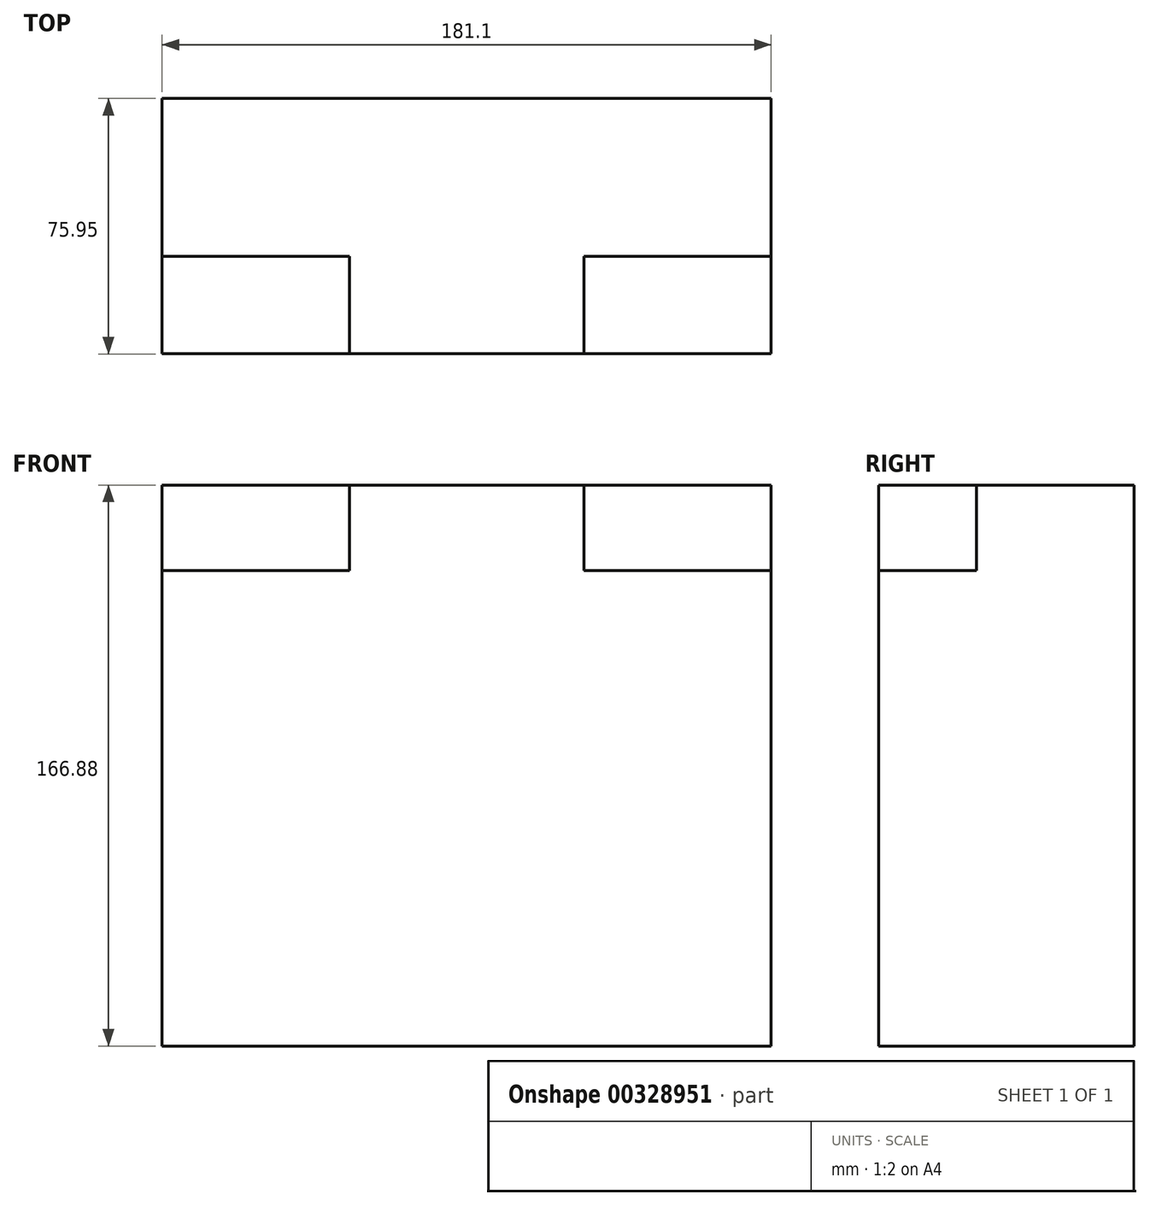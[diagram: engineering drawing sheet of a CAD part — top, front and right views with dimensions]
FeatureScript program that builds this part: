
annotation { "Feature Type Name" : "Feature", "Feature Type Description" : "" }
export const myFeature = defineFeature(function(context is Context, id is Id, definition is map)
    precondition{}
    {
        {
            var Q0;
            Q0=qCreatedBy(makeId("Front.planeOp"),FACE);
            var sketch = newSketch(context, id + "F0", { "sketchPlane" : qUnion([Q0])});
            skLineSegment(sketch, "E0.bottom", {"start": v(90.55, -83.44) * mm, "end": v(-90.55, -83.44) * mm});
            skLineSegment(sketch, "E0.top", {"start": v(90.55, 83.44) * mm, "end": v(-90.55, 83.44) * mm});
            skLineSegment(sketch, "E0.left", {"start": v(90.55, -83.44) * mm, "end": v(90.55, 83.44) * mm});
            skLineSegment(sketch, "E0.right", {"start": v(-90.55, -83.44) * mm, "end": v(-90.55, 83.44) * mm});
            skPoint(sketch, "E0.middle", {"position": v(0, 0) * mm});
            skSolve(sketch);
        }
        {
            var Q0;
            Q0=makeQuery(id+"F0.imprint","IMPRINT",FACE,{"disambiguationData":[TD([[makeQuery(id+"F0.imprint","IMPRINT",EDGE,{"derivedFrom":sQuery(id+"F0.wireOp",EDGE,"E0.bottom")}),-1.0]])]});
            extrude(context, id + "F1", {"entities" : qUnion([Q0]), "depth" : 75.95 * mm});
        }
        {
            var Q0;
            Q0=makeQuery(id+"F1.opExtrude","SWEPT_FACE",FACE,{"disambiguationData":[OSD([sQuery(id+"F0.wireOp",EDGE,"E0.top")])]});
            var sketch = newSketch(context, id + "F2", { "sketchPlane" : qUnion([Q0])});
            skLineSegment(sketch, "E1.bottom", {"start": v(-90.55, -46.98) * mm, "end": v(-34.86, -46.98) * mm});
            skLineSegment(sketch, "E1.top", {"start": v(-90.55, -75.95) * mm, "end": v(-34.86, -75.95) * mm});
            skLineSegment(sketch, "E1.left", {"start": v(-90.55, -46.98) * mm, "end": v(-90.55, -75.95) * mm});
            skLineSegment(sketch, "E1.right", {"start": v(-34.86, -46.98) * mm, "end": v(-34.86, -75.95) * mm});
            skLineSegment(sketch, "E2.MirrorCS", {"start": v(90.55, -46.98) * mm, "end": v(34.86, -46.98) * mm});
            skLineSegment(sketch, "E3.MirrorCS", {"start": v(34.86, -46.98) * mm, "end": v(34.86, -75.95) * mm});
            skLineSegment(sketch, "E4.MirrorCS", {"start": v(90.55, -75.95) * mm, "end": v(34.86, -75.95) * mm});
            skLineSegment(sketch, "E5.MirrorCS", {"start": v(90.55, -46.98) * mm, "end": v(90.55, -75.95) * mm});
            skSolve(sketch);
        }
        {
            var Q0;
            Q0=makeQuery(id+"F2.imprint","IMPRINT",FACE,{"disambiguationData":[TD([[makeQuery(id+"F2.imprint","IMPRINT",EDGE,{"derivedFrom":sQuery(id+"F2.wireOp",EDGE,"E1.bottom")}),-1.0]])]});
            var Q1;
            Q1=makeQuery(id+"F2.imprint","IMPRINT",FACE,{"disambiguationData":[TD([[makeQuery(id+"F2.imprint","IMPRINT",EDGE,{"derivedFrom":sQuery(id+"F2.wireOp",EDGE,"E2.MirrorCS")}),1.0]])]});
            extrude(context, id + "F3", {"entities" : qUnion([Q0, Q1]), "operationType" : NewBodyOperationType.REMOVE, "oppositeDirection" : true, "depth" : 25.4 * mm});
        }
    });
